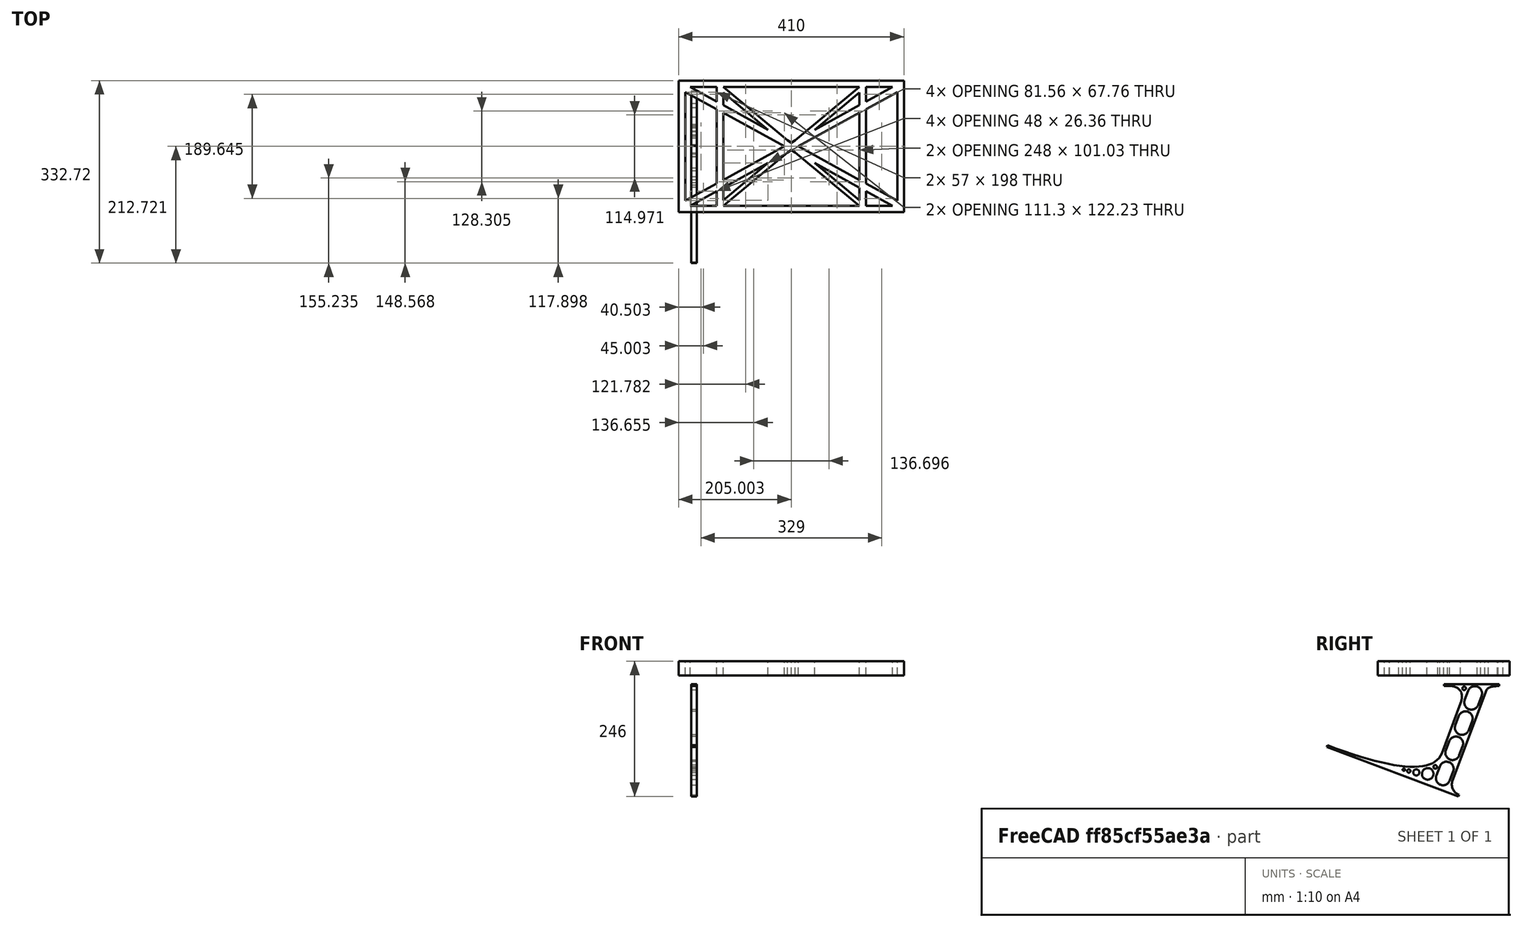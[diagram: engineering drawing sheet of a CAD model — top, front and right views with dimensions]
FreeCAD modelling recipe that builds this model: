
FCSTD DOCUMENT  (FreeCAD 0.19R0.19.2)
Label: laptopStand036
License: All rights reserved
LicenseURL: http://en.wikipedia.org/wiki/All_rights_reserved
objects: Sketcher::SketchObject×2, Part::Extrusion×2
note: 4 computed .brp shape members not serialized (recipe doc carries the construction recipe); baked Part::Feature solids carry a one-line shape summary decoded from their .brp

FEATURE [Sketcher::SketchObject] Sketch
  FullyConstrained = true
  sketch-geometry (52):
    g0: LineSegment StartX=-22.9272 StartY=136.221 StartZ=0 EndX=-22.9272 EndY=-103.779 EndZ=0
    g1: LineSegment StartX=-22.9272 StartY=136.221 StartZ=0 EndX=387.073 EndY=136.221 EndZ=0
    g2: LineSegment StartX=-22.9272 StartY=-103.779 StartZ=0 EndX=387.073 EndY=-103.779 EndZ=0
    g3: LineSegment StartX=387.073 StartY=136.221 StartZ=0 EndX=387.073 EndY=-103.779 EndZ=0
    g4: LineSegment StartX=375.073 StartY=115.221 StartZ=0 EndX=318.073 EndY=83.9235 EndZ=0
    g5: LineSegment StartX=-10.9272 StartY=-82.7794 StartZ=0 EndX=46.0728 EndY=-51.4823 EndZ=0
    g6: LineSegment StartX=-1.92719 StartY=124.221 StartZ=0 EndX=46.0728 EndY=97.8651 EndZ=0
    g7: LineSegment StartX=366.073 StartY=-91.7794 StartZ=0 EndX=318.073 EndY=-65.424 EndZ=0
    g8: LineSegment StartX=-10.9272 StartY=115.221 StartZ=0 EndX=-10.9272 EndY=-82.7794 EndZ=0
    g9: LineSegment StartX=375.073 StartY=-82.7794 StartZ=0 EndX=375.073 EndY=115.221 EndZ=0
    g10: LineSegment StartX=-1.92719 StartY=-91.7794 StartZ=0 EndX=46.0728 EndY=-91.7794 EndZ=0
    g11: LineSegment StartX=318.073 StartY=124.221 StartZ=0 EndX=366.073 EndY=124.221 EndZ=0
    g12: LineSegment StartX=306.073 StartY=-81.8102 StartZ=0 EndX=224.513 EndY=-14.0532 EndZ=0
    g13: LineSegment StartX=58.0728 StartY=114.251 StartZ=0 EndX=139.632 EndY=46.4944 EndZ=0
    g14: LineSegment StartX=306.073 StartY=124.221 StartZ=0 EndX=189.124 EndY=27.0628 EndZ=0
    g15: LineSegment StartX=58.0728 StartY=-91.7794 StartZ=0 EndX=175.022 EndY=5.37834 EndZ=0
    g16: LineSegment StartX=46.0728 StartY=124.221 StartZ=0 EndX=46.0728 EndY=97.8651 EndZ=0
    g17: LineSegment StartX=58.0728 StartY=-81.8102 StartZ=0 EndX=58.0728 EndY=-58.8351 EndZ=0
    g18: LineSegment StartX=318.073 StartY=124.221 StartZ=0 EndX=318.073 EndY=97.8651 EndZ=0
    g19: LineSegment StartX=306.073 StartY=114.251 StartZ=0 EndX=306.073 EndY=91.2763 EndZ=0
    g20: LineSegment StartX=182.073 StartY=23.1914 StartZ=0 EndX=189.124 EndY=27.0628 EndZ=0
    g21: LineSegment StartX=182.073 StartY=9.24976 StartZ=0 EndX=175.022 EndY=5.37834 EndZ=0
    g22: LineSegment StartX=224.513 StartY=46.4944 StartZ=0 EndX=306.073 EndY=114.251 EndZ=0
    g23: LineSegment StartX=175.022 StartY=27.0628 StartZ=0 EndX=58.0728 EndY=124.221 EndZ=0
    g24: LineSegment StartX=169.377 StartY=16.2206 StartZ=0 EndX=58.0728 EndY=77.3346 EndZ=0
    g25: LineSegment StartX=139.632 StartY=-14.0532 StartZ=0 EndX=58.0728 EndY=-81.8102 EndZ=0
    g26: LineSegment StartX=194.768 StartY=16.2206 StartZ=0 EndX=306.073 EndY=-44.8935 EndZ=0
    g27: LineSegment StartX=224.513 StartY=46.4944 StartZ=0 EndX=306.073 EndY=91.2763 EndZ=0
    g28: LineSegment StartX=175.022 StartY=27.0628 StartZ=0 EndX=182.073 EndY=23.1914 EndZ=0
    g29: LineSegment StartX=139.632 StartY=-14.0532 StartZ=0 EndX=58.0728 EndY=-58.8351 EndZ=0
    g30: LineSegment StartX=189.124 StartY=5.37834 StartZ=0 EndX=182.073 EndY=9.24976 EndZ=0
    g31: LineSegment StartX=189.124 StartY=5.37834 StartZ=0 EndX=306.073 EndY=-91.7794 EndZ=0
    g32: LineSegment StartX=306.073 StartY=77.3346 StartZ=0 EndX=306.073 EndY=-44.8935 EndZ=0
    g33: LineSegment StartX=318.073 StartY=83.9235 StartZ=0 EndX=318.073 EndY=-51.4823 EndZ=0
    g34: LineSegment StartX=318.073 StartY=97.8651 StartZ=0 EndX=366.073 EndY=124.221 EndZ=0
    g35: LineSegment StartX=306.073 StartY=77.3346 StartZ=0 EndX=194.768 EndY=16.2206 EndZ=0
    g36: LineSegment StartX=306.073 StartY=-58.8351 StartZ=0 EndX=224.513 EndY=-14.0532 EndZ=0
    g37: LineSegment StartX=306.073 StartY=-58.8351 StartZ=0 EndX=306.073 EndY=-81.8102 EndZ=0
    g38: LineSegment StartX=318.073 StartY=-51.4823 StartZ=0 EndX=375.073 EndY=-82.7794 EndZ=0
    g39: LineSegment StartX=318.073 StartY=-65.424 StartZ=0 EndX=318.073 EndY=-91.7794 EndZ=0
    g40: LineSegment StartX=306.073 StartY=124.221 StartZ=0 EndX=58.0728 EndY=124.221 EndZ=0
    g41: LineSegment StartX=318.073 StartY=-91.7794 StartZ=0 EndX=366.073 EndY=-91.7794 EndZ=0
    g42: LineSegment StartX=58.0728 StartY=-91.7794 StartZ=0 EndX=306.073 EndY=-91.7794 EndZ=0
    g43: LineSegment StartX=58.0728 StartY=-44.8935 StartZ=0 EndX=58.0728 EndY=77.3346 EndZ=0
    g44: LineSegment StartX=46.0728 StartY=-65.424 StartZ=0 EndX=-1.92719 EndY=-91.7794 EndZ=0
    g45: LineSegment StartX=46.0728 StartY=-65.424 StartZ=0 EndX=46.0728 EndY=-91.7794 EndZ=0
    g46: LineSegment StartX=58.0728 StartY=-44.8935 StartZ=0 EndX=169.377 EndY=16.2206 EndZ=0
    g47: LineSegment StartX=58.0728 StartY=91.2763 StartZ=0 EndX=58.0728 EndY=114.251 EndZ=0
    g48: LineSegment StartX=46.0728 StartY=83.9235 StartZ=0 EndX=46.0728 EndY=-51.4823 EndZ=0
    g49: LineSegment StartX=46.0728 StartY=124.221 StartZ=0 EndX=-1.92719 EndY=124.221 EndZ=0
    g50: LineSegment StartX=58.0728 StartY=91.2763 StartZ=0 EndX=139.632 EndY=46.4944 EndZ=0
    g51: LineSegment StartX=46.0728 StartY=83.9235 StartZ=0 EndX=-10.9272 EndY=115.221 EndZ=0
  constraints (102):
    c: Vertical(g0)
    c: Distance(g0) = 240
    c: Horizontal(g1)
    c: Distance(g1) = 410
    c: Coincident(g1,g0)
    c: Coincident(g2,g0)
    c: Horizontal(g2)
    c: Coincident(g3,g1)
    c: Vertical(g3)
    c: Coincident(g2,g3)
    c: Block(g1)
    c: Horizontal(g10)
    c: Horizontal(g11)
    c: PointOnObject(g35,g6)
    c: Coincident(g28,g20)
    c: Coincident(g30,g21)
    c: Tangent(g7,g24)
    c: PointOnObject(g24,g5)
    c: PointOnObject(g26,g4)
    c: Coincident(g20,g14)
    c: Tangent(g20,g27)
    c: Coincident(g50,g13)
    c: Coincident(g28,g23)
    c: Coincident(g22,g27)
    c: Coincident(g21,g15)
    c: Coincident(g29,g25)
    c: Tangent(g21,g29)
    c: Coincident(g36,g12)
    c: Coincident(g31,g30)
    c: Coincident(g22,g19)
    c: Tangent(g19,g32)
    c: Tangent(g18,g33)
    c: Coincident(g27,g19)
    c: Tangent(g27,g34)
    c: Coincident(g4,g33)
    c: Coincident(g35,g32)
    c: Tangent(g4,g35)
    c: Coincident(g37,g12)
    c: Tangent(g7,g36)
    c: Tangent(g32,g37)
    c: Coincident(g26,g32)
    c: Tangent(g26,g38)
    c: Coincident(g33,g38)
    c: Coincident(g39,g7)
    c: Tangent(g33,g39)
    c: Coincident(g25,g17)
    c: Tangent(g17,g43)
    c: Coincident(g29,g17)
    c: Tangent(g29,g44)
    c: Coincident(g45,g44)
    c: Tangent(g16,g45)
    c: Coincident(g5,g48)
    c: Coincident(g46,g43)
    c: Tangent(g5,g46)
    c: Tangent(g43,g47)
    c: Tangent(g16,g48)
    c: Coincident(g13,g47)
    c: PointOnObject(g40,g23)
    c: Tangent(g40,g49)
    c: Coincident(g6,g16)
    c: Coincident(g50,g47)
    c: Tangent(g6,g50)
    c: Coincident(g24,g43)
    c: Coincident(g51,g48)
    c: Tangent(g24,g51)
    c: Block(g23)
    c: Block(g14)
    c: Block(g20)
    c: Block(g40)
    c: Block(g18)
    c: Block(g34)
    c: Block(g4)
    c: Block(g38)
    c: Block(g9)
    c: Block(g36)
    c: Block(g37)
    c: Block(g7)
    c: Block(g39)
    c: Block(g22)
    c: Block(g31)
    c: Block(g42)
    c: Block(g21)
    c: Block(g15)
    c: Block(g29)
    c: Block(g25)
    c: Block(g45)
    c: Block(g44)
    c: Block(g5)
    c: Block(g8)
    c: Block(g51)
    c: Block(g6)
    c: Block(g16)
    c: Block(g13)
    c: Block(g47)
    c: Block(g35)
    c: Block(g32)
    c: Block(g24)
    c: Block(g46)
    c: Block(g49)
    c: Block(g11)
    c: Block(g41)
    c: Block(g10)
FEATURE [Part::Extrusion] Extrude
  Base = -> Sketch
  Dir = (0,0,1)
  DirMode = 2
  FaceMakerClass = Part::FaceMakerBullseye
  LengthFwd = 26
  LengthRev = 0
  Solid = true
  Symmetric = false
FEATURE [Sketcher::SketchObject] Sketch001
  FullyConstrained = true
  MapMode = 4
  Placement = pos=(0,0,0) rot=(0.57735,0.57735,0.57735;2.0944rad)
  Support = -> [Sketch]
  sketch-geometry (46):
    g0: BSplineCurve PolesCount=3 KnotsCount=2 Degree=2 IsPeriodic=0
    g1: ArcOfCircle CenterX=73.122 CenterY=-32.2909 CenterZ=0 NormalX=0 NormalY=0 NormalZ=1 AngleXU=0 Radius=13 StartAngle=5.92268 EndAngle=9.06428
    g2: ArcOfCircle CenterX=66.7816 CenterY=-49.1439 CenterZ=0 NormalX=0 NormalY=0 NormalZ=1 AngleXU=0 Radius=13 StartAngle=2.78068 EndAngle=5.92131
    g3: ArcOfCircle CenterX=55.9263 CenterY=-78.1807 CenterZ=0 NormalX=0 NormalY=0 NormalZ=1 AngleXU=0 Radius=13 StartAngle=5.92268 EndAngle=9.06428
    g4: ArcOfCircle CenterX=49.5884 CenterY=-95.0342 CenterZ=0 NormalX=0 NormalY=0 NormalZ=1 AngleXU=0 Radius=13 StartAngle=2.78068 EndAngle=5.92131
    g5: ArcOfCircle CenterX=38.7206 CenterY=-124.067 CenterZ=0 NormalX=0 NormalY=0 NormalZ=1 AngleXU=0 Radius=13 StartAngle=5.92268 EndAngle=9.06428
    g6: ArcOfCircle CenterX=32.3875 CenterY=-140.92 CenterZ=0 NormalX=0 NormalY=0 NormalZ=1 AngleXU=0 Radius=13 StartAngle=2.78068 EndAngle=5.92131
    g7: ArcOfCircle CenterX=21.4715 CenterY=-169.934 CenterZ=0 NormalX=0 NormalY=0 NormalZ=1 AngleXU=0 Radius=13 StartAngle=5.92268 EndAngle=9.06428
    g8: ArcOfCircle CenterX=15.1336 CenterY=-186.787 CenterZ=0 NormalX=0 NormalY=0 NormalZ=1 AngleXU=0 Radius=13 StartAngle=2.78068 EndAngle=5.92131
    g9-g12: Circle x4 (B-spline internal-alignment scaffolding for g13; pole/knot coordinates omitted)
    g13: BSplineCurve PolesCount=4 KnotsCount=2 Degree=3 IsPeriodic=0
    g14: GeomPoint X=28.8094 Y=-19.0875 Z=0
    g15: GeomPoint X=47.0443 Y=-50.4712 Z=0
    g16: Circle CenterX=53.5586 CenterY=-23.2695 CenterZ=0 NormalX=0 NormalY=0 NormalZ=1 AngleXU=0 Radius=3.24518
    g17: Circle CenterX=-195.441 CenterY=-127.082 CenterZ=0 NormalX=0 NormalY=0 NormalZ=1 AngleXU=0 Radius=1
    g18: Circle CenterX=-8.24091 CenterY=-197.481 CenterZ=0 NormalX=0 NormalY=0 NormalZ=1 AngleXU=0 Radius=1
    g19: Circle CenterX=12.8789 CenterY=-141.321 CenterZ=0 NormalX=0 NormalY=0 NormalZ=1 AngleXU=0 Radius=1
    g20: BSplineCurve PolesCount=3 KnotsCount=2 Degree=2 IsPeriodic=0
    g21: GeomPoint X=-195.441 Y=-127.082 Z=0
    g22: GeomPoint X=12.8789 Y=-141.321 Z=0
    g23: Circle CenterX=-12.8016 CenterY=-179.036 CenterZ=0 NormalX=0 NormalY=0 NormalZ=1 AngleXU=0 Radius=10.5072
    g24: Circle CenterX=0.933922 CenterY=-166.43 CenterZ=0 NormalX=0 NormalY=0 NormalZ=1 AngleXU=0 Radius=3.26661
    g25: Circle CenterX=-33.5518 CenterY=-176.44 CenterZ=0 NormalX=0 NormalY=0 NormalZ=1 AngleXU=0 Radius=5.64388
    g26: Circle CenterX=-47.2366 CenterY=-173.859 CenterZ=0 NormalX=0 NormalY=0 NormalZ=1 AngleXU=0 Radius=3.01653
    g27: Circle CenterX=-56.2595 CenterY=-171.456 CenterZ=0 NormalX=0 NormalY=0 NormalZ=1 AngleXU=0 Radius=2.12826
    g28: ArcOfCircle CenterX=51.2151 CenterY=-198.473 CenterZ=0 NormalX=0 NormalY=0 NormalZ=1 AngleXU=0 Radius=20 StartAngle=2.78189 EndAngle=4.35269
    g29: LineSegment StartX=32.4951 StartY=-191.433 StartZ=0 EndX=94.6577 EndY=-26.1351 EndZ=0
    g30: LineSegment StartX=43.1192 StartY=-220.001 StartZ=0 EndX=-196.497 EndY=-129.89 EndZ=0
    g31: LineSegment StartX=43.1192 StartY=-220.001 StartZ=0 EndX=44.1752 EndY=-217.193 EndZ=0
    g32: LineSegment StartX=117.223 StartY=-19.0875 StartZ=0 EndX=117.223 EndY=-16.0875 EndZ=0
    g33: LineSegment StartX=117.223 StartY=-16.0875 StartZ=0 EndX=17.2232 EndY=-16.0875 EndZ=0
    g34: LineSegment StartX=17.2232 StartY=-16.0875 StartZ=0 EndX=17.2232 EndY=-19.0875 EndZ=0
    g35: LineSegment StartX=28.8094 StartY=-19.0875 StartZ=0 EndX=17.2232 EndY=-19.0875 EndZ=0
    g36: LineSegment StartX=47.0443 StartY=-50.4712 StartZ=0 EndX=12.8789 EndY=-141.321 EndZ=0
    g37: LineSegment StartX=-195.441 StartY=-127.082 StartZ=0 EndX=-196.497 EndY=-129.89 EndZ=0
    g38: LineSegment StartX=85.2864 StartY=-36.8765 StartZ=0 EndX=78.9396 EndY=-53.7463 EndZ=0
    g39: LineSegment StartX=60.9577 StartY=-27.7052 StartZ=0 EndX=54.6191 EndY=-44.5532 EndZ=0
    g40: LineSegment StartX=68.0907 StartY=-82.7664 StartZ=0 EndX=61.7465 EndY=-99.6365 EndZ=0
    g41: LineSegment StartX=43.7619 StartY=-73.595 StartZ=0 EndX=37.426 EndY=-90.4435 EndZ=0
    g42: LineSegment StartX=50.885 StartY=-128.652 StartZ=0 EndX=44.5456 EndY=-145.522 EndZ=0
    g43: LineSegment StartX=26.5562 StartY=-119.481 StartZ=0 EndX=20.2251 EndY=-136.329 EndZ=0
    g44: LineSegment StartX=9.3071 StartY=-165.349 StartZ=0 EndX=2.97115 EndY=-182.197 EndZ=0
    g45: LineSegment StartX=33.6358 StartY=-174.52 StartZ=0 EndX=27.2917 EndY=-191.39 EndZ=0
  constraints (69):
    c: Block(g0)
    c: Block(g1)
    c: Block(g2)
    c: Block(g4)
    c: Block(g3)
    c: Block(g6)
    c: Block(g5)
    c: Block(g8)
    c: Block(g7)
    c: Weight(g9) = 1
    c: Equal(g9,g10)
    c: Equal(g9,g11)
    c: Equal(g9,g12)
    c: InternalAlignment(g9-g12 -> g13) x4
    c: InternalAlignment(g14,g13)
    c: InternalAlignment(g15,g13)
    c: Block(g16)
    c: Weight(g17) = 1
    c: Equal(g17,g18)
    c: Equal(g17,g19)
    c: InternalAlignment(g17,g20)
    c: InternalAlignment(g18,g20)
    c: InternalAlignment(g19,g20)
    c: InternalAlignment(g21,g20)
    c: InternalAlignment(g22,g20)
    c: Block(g20)
    c: Block(g23)
    c: Block(g24)
    c: Block(g25)
    c: Block(g26)
    c: Block(g27)
    c: Block(g28)
    c: Coincident(g29,g28)
    c: Coincident(g29,g0)
    c: Block(g13)
    c: Coincident(g31,g30)
    c: Coincident(g31,g28)
    c: Block(g31)
    c: Coincident(g32,g0)
    c: Vertical(g32)
    c: Coincident(g33,g32)
    c: Horizontal(g33)
    c: Coincident(g34,g33)
    c: Vertical(g34)
    c: Block(g33)
    c: Coincident(g35,g13)
    c: Coincident(g35,g34)
    c: Horizontal(g35)
    c: Coincident(g36,g13)
    c: Coincident(g36,g20)
    c: Coincident(g37,g20)
    c: Coincident(g37,g30)
    c: Block(g30)
    c: Coincident(g38,g1)
    c: Coincident(g38,g2)
    c: Coincident(g39,g1)
    c: Coincident(g39,g2)
    c: Coincident(g40,g3)
    c: Coincident(g40,g4)
    c: Coincident(g41,g3)
    c: Coincident(g41,g4)
    c: Coincident(g42,g5)
    c: Coincident(g42,g6)
    c: Coincident(g43,g5)
    c: Coincident(g43,g6)
    c: Coincident(g44,g7)
    c: Coincident(g44,g8)
    c: Coincident(g45,g7)
    c: Coincident(g45,g8)
FEATURE [Part::Extrusion] Extrude001
  Base = -> Sketch001
  Dir = (1,0,0)
  DirMode = 2
  FaceMakerClass = Part::FaceMakerBullseye
  LengthFwd = 10
  LengthRev = 0
  Solid = true
  Symmetric = false
